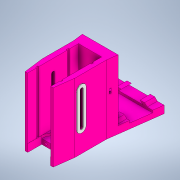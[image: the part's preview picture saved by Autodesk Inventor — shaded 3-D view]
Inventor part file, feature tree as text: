
AUTODESK INVENTOR PART (.ipt)
format: ipt  version: 2020 (Build 240168000, 168)  size: 528,384 bytes
history: native  units: mm
features: sketch x16, extrude x15, mirror x3, fillet x2, sweep x1, chamfer x1
ambient origin geometry x8: Origin, YZ Plane, XZ Plane, XY Plane, X Axis, Y Axis, Z Axis, Center Point
bodies: Solid1 (feature_tree), Solid3 (feature_tree)
feature tree (38):
  sketch  "Sketch1"  dims[d0=45.0mm d1=100.0mm]
  extrude  "Extrusion1"  Depth=100.0mm
  extrude  "Extrusion2"  Depth=5.0mm
  extrude  "Extrusion3"  Depth=120.0mm TaperAngle=0.0deg
  extrude  "Extrusion4"  Depth=11.0mm
  sweep  "Sweep1"
  extrude  "Extrusion5"  Depth=2.0mm
  extrude  "Extrusion6"  Depth=28.0mm
  extrude  "Extrusion7"  Depth=30.0mm
  extrude  "Extrusion8"  TaperAngle=0.0deg  [1 undecoded]
  extrude  "Extrusion9"  Depth=5.0mm
  extrude  "Extrusion10"  Depth=10.0mm
  mirror  "Mirror1"
  mirror  "Mirror2"
  extrude  "Extrusion13"  TaperAngle=45.0deg  [1 undecoded]
  extrude  "Extrusion14"  TaperAngle=0.0deg  [1 undecoded]
  mirror  "Mirror4"
  extrude  "Extrusion15"  Depth=5.0mm
  extrude  "Extrusion16"  Depth=25.0mm
  extrude  "Extrusion17"  Depth=10.0mm
  chamfer  "Chamfer1"  [1 undecoded]
  fillet  "Fillet1"  Radius=80.0mm
  fillet  "Fillet2"  Radius=9.0mm
  sketch  "Sketch2"  dims[d2=17.01696mm d3=5.0mm]
  sketch  "Sketch3"  dims[d5=20.0mm d7=120.0mm d8=0.0mm]
  sketch  "Sketch5"  dims[d9=15.0mm d10=0.0mm d11=11.0mm]
  sketch  "Sketch6"  dims[d12=22.5mm d13=10.0mm]
  sketch  "Sketch7"  dims[d15=10.0mm d16=2.0mm]
  sketch  "Sketch8"  dims[d17=4.0mm d20=28.0mm]
  sketch  "Sketch9"  dims[d21=6.0mm d22=30.0mm]
  sketch  "Sketch10"  dims[d23=25.0mm d24=0.0mm d25=0.0mm]
  sketch  "Sketch11"  dims[d26=40.0mm d27=5.0mm]
  sketch  "Sketch12"  dims[d29=10.532mm d30=0.0mm d32=10.0mm]
  sketch  "Sketch15"  dims[d33=0.0mm d34=45.0deg]
  sketch  "Sketch16"  dims[d35=5.0mm d36=0.0mm d37=0.0mm]
  sketch  "Sketch17"  dims[d38=5.0mm d39=5.0mm]
  sketch  "Sketch18"  dims[d40=20.0mm d41=25.0mm]
  sketch  "Sketch19"  dims[d42=25.0mm d43=10.0mm d44=0.0mm d45=0.0mm d46=80.0mm d47=9.0mm d48=5.0mm d49=0.0mm d57=1.0mm d58=1.0mm d59=1.0mm d60=5.0mm d61=0.0mm d65=8.5mm d66=5.0mm d67=4.4mm d68=30.0mm d69=0.0mm d70=8.0mm d71=4.5mm d72=8.5mm d73=5.0mm d74=9.0mm d75=0.0mm d76=18.0mm d77=1.0mm d78=0.0mm d87=9.0mm d88=60.0mm d89=10.0mm d90=3.5mm d91=0.0mm d92=3.5mm d93=5.0mm d94=0.0mm d95=0.4mm d96=0.4mm d97=0.4mm d98=0.4mm d99=0.4mm d100=0.4mm d101=1.0mm d102=10.0mm d103=0.0mm d104=0.2mm d105=0.2mm d106=0.2mm d107=0.2mm d108=0.2mm d109=0.2mm d110=0.2mm d111=0.2mm d112=0.2mm d113=0.2mm d114=0.2mm d115=0.2mm d116=10.0mm d117=0.0mm d118=0.2mm d119=0.2mm d120=0.2mm d121=116.0mm d122=0.4mm d123=0.0mm d124=0.0mm d125=2.0mm d126=2.0mm d127=45.0deg d128=6.0mm d129=2.0mm]
note: 4 required parameter values undecoded (feature->parameter linkage not recoverable at this tier; creation-order binding heuristic only, values carry confidence <= 0.55)
